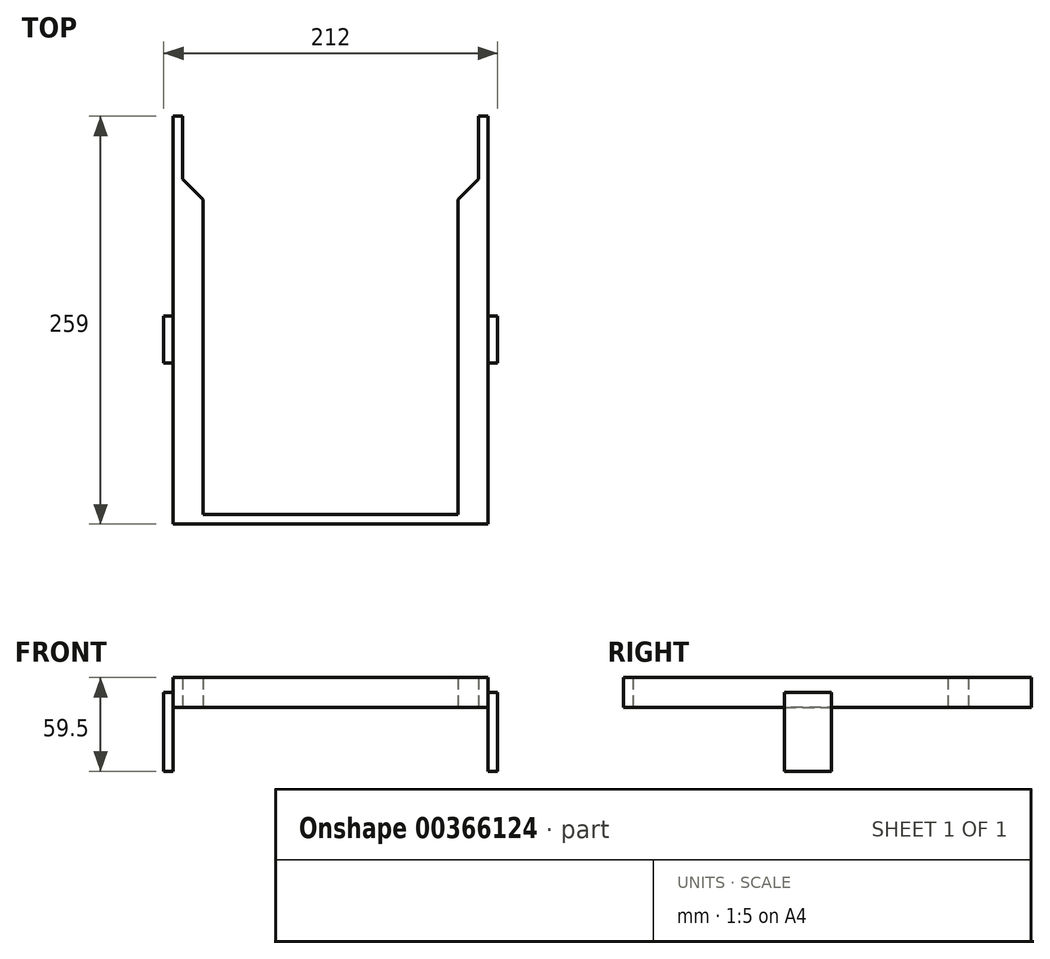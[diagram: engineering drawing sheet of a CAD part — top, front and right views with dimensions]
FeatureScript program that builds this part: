
annotation { "Feature Type Name" : "Feature", "Feature Type Description" : "" }
export const myFeature = defineFeature(function(context is Context, id is Id, definition is map)
    precondition{}
    {
        {
            var Q0;
            Q0=qCreatedBy(makeId("Top.planeOp"),FACE);
            var sketch = newSketch(context, id + "F0", { "sketchPlane" : qUnion([Q0])});
            skLineSegment(sketch, "E0", {"start": v(-94, 20) * mm, "end": v(-94, -20) * mm});
            skLineSegment(sketch, "E1", {"start": v(-81, -33) * mm, "end": v(-94, -20) * mm});
            skLineSegment(sketch, "E2", {"start": v(-81, -33) * mm, "end": v(-81, -233) * mm});
            skLineSegment(sketch, "E3", {"start": v(-81, -233) * mm, "end": v(0, -233) * mm});
            skLineSegment(sketch, "E4", {"start": v(0, -233) * mm, "end": v(0, -239) * mm});
            skLineSegment(sketch, "E5", {"start": v(0, -239) * mm, "end": v(-100, -239) * mm});
            skLineSegment(sketch, "E6", {"start": v(-100, -239) * mm, "end": v(-100, 20) * mm});
            skLineSegment(sketch, "E7", {"start": v(-100, 20) * mm, "end": v(-94, 20) * mm});
            skLineSegment(sketch, "E8", {"start": v(-100, -106.8) * mm, "end": v(-106, -106.8) * mm});
            skLineSegment(sketch, "E9", {"start": v(-106, -106.8) * mm, "end": v(-106, -136.8) * mm});
            skLineSegment(sketch, "E10", {"start": v(-106, -136.8) * mm, "end": v(-100, -136.8) * mm});
            skLineSegment(sketch, "E11.MirrorCS", {"start": v(106, -136.8) * mm, "end": v(100, -136.8) * mm});
            skLineSegment(sketch, "E12.MirrorCS", {"start": v(100, -106.8) * mm, "end": v(106, -106.8) * mm});
            skLineSegment(sketch, "E13.MirrorCS", {"start": v(100, 20) * mm, "end": v(94, 20) * mm});
            skLineSegment(sketch, "E14.MirrorCS", {"start": v(81, -33) * mm, "end": v(94, -20) * mm});
            skLineSegment(sketch, "E15.MirrorCS", {"start": v(106, -106.8) * mm, "end": v(106, -136.8) * mm});
            skLineSegment(sketch, "E16.MirrorCS", {"start": v(100, -239) * mm, "end": v(100, 20) * mm});
            skLineSegment(sketch, "E17.MirrorCS", {"start": v(0, -239) * mm, "end": v(100, -239) * mm});
            skLineSegment(sketch, "E18.MirrorCS", {"start": v(81, -233) * mm, "end": v(0, -233) * mm});
            skLineSegment(sketch, "E19.MirrorCS", {"start": v(94, 20) * mm, "end": v(94, -20) * mm});
            skLineSegment(sketch, "E20.MirrorCS", {"start": v(81, -33) * mm, "end": v(81, -233) * mm});
            skSolve(sketch);
        }
        {
            var Q0;
            Q0=makeQuery(id+"F0.imprint","IMPRINT",FACE,{"disambiguationData":[TD([[makeQuery(id+"F0.imprint","IMPRINT",EDGE,{"derivedFrom":sQuery(id+"F0.wireOp",EDGE,"E0")}),-1.0]])]});
            var Q1;
            {var subQ3=sQuery(id+"F0.wireOp",EDGE,"E13.MirrorCS");Q1=makeQuery(id+"F0.imprint","IMPRINT",FACE,{"disambiguationData":[TD([[makeQuery(id+"F0.imprint","IMPRINT",EDGE,{"derivedFrom":subQ3}),1.0]])]});}
            extrude(context, id + "F1", {"entities" : qUnion([Q0, Q1]), "depth" : 9.5 * mm, "hasSecondDirection" : true, "secondDirectionOppositeDirection" : true, "secondDirectionDepth" : 9.5 * mm});
        }
        {
            var Q0;
            {var subQ0=sQuery(id+"F0.wireOp",EDGE,"E8");Q0=makeQuery(id+"F0.imprint","IMPRINT",FACE,{"disambiguationData":[TD([[makeQuery(id+"F0.imprint","IMPRINT",EDGE,{"derivedFrom":subQ0}),1.0]])]});}
            var Q1;
            {var subQ0=sQuery(id+"F0.wireOp",EDGE,"E11.MirrorCS");Q1=makeQuery(id+"F0.imprint","IMPRINT",FACE,{"disambiguationData":[TD([[makeQuery(id+"F0.imprint","IMPRINT",EDGE,{"derivedFrom":subQ0}),-1.0]])]});}
            extrude(context, id + "F2", {"entities" : qUnion([Q0, Q1]), "operationType" : NewBodyOperationType.ADD, "oppositeDirection" : true, "depth" : 50 * mm});
        }
    });
